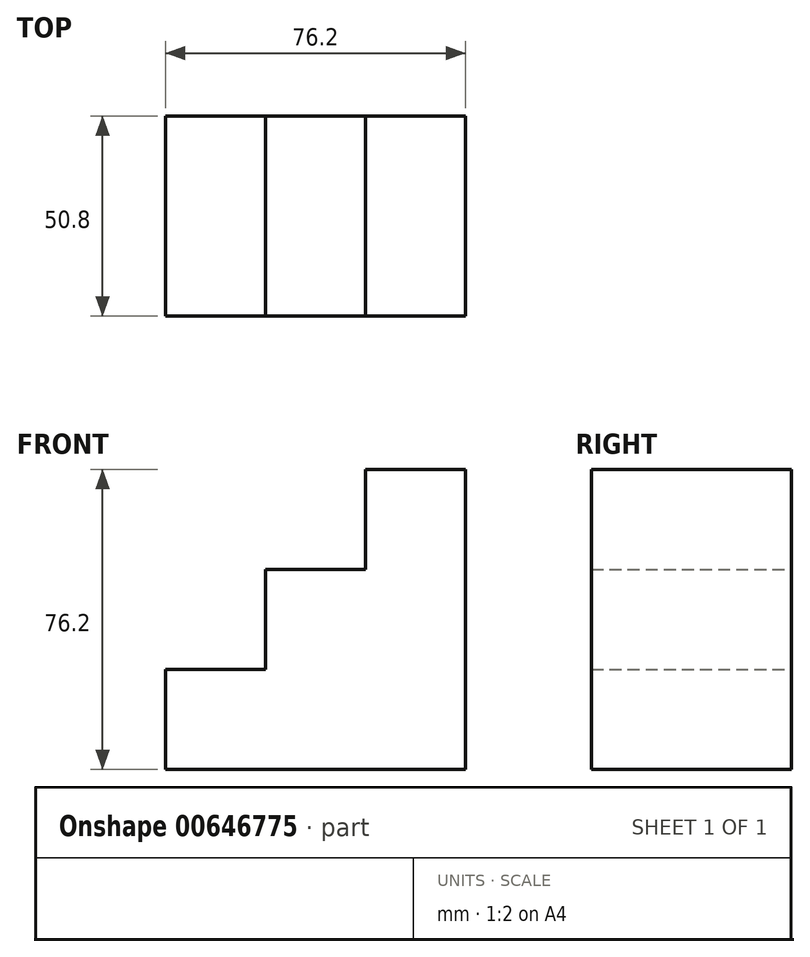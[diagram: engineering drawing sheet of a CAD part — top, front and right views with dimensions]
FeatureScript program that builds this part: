
annotation { "Feature Type Name" : "Feature", "Feature Type Description" : "" }
export const myFeature = defineFeature(function(context is Context, id is Id, definition is map)
    precondition{}
    {
        {
            var Q0;
            Q0=qCreatedBy(makeId("Front.planeOp"),FACE);
            var sketch = newSketch(context, id + "F0", { "sketchPlane" : qUnion([Q0])});
            skLineSegment(sketch, "E0", {"start": v(48.03, 47.46) * mm, "end": v(48.03, -28.74) * mm});
            skLineSegment(sketch, "E1", {"start": v(48.03, -28.74) * mm, "end": v(-28.17, -28.74) * mm});
            skLineSegment(sketch, "E2", {"start": v(-28.17, -28.74) * mm, "end": v(-28.17, -3.34) * mm});
            skLineSegment(sketch, "E3", {"start": v(-28.17, -3.34) * mm, "end": v(-2.77, -3.34) * mm});
            skLineSegment(sketch, "E4", {"start": v(-2.77, -3.34) * mm, "end": v(-2.77, 22.06) * mm});
            skLineSegment(sketch, "E5", {"start": v(-2.77, 22.06) * mm, "end": v(22.63, 22.06) * mm});
            skLineSegment(sketch, "E6", {"start": v(22.63, 22.06) * mm, "end": v(22.63, 47.46) * mm});
            skLineSegment(sketch, "E7", {"start": v(22.63, 47.46) * mm, "end": v(48.03, 47.46) * mm});
            skSolve(sketch);
        }
        {
            var Q0;
            Q0=makeQuery(id+"F0.imprint","IMPRINT",FACE,{"disambiguationData":[TD([[makeQuery(id+"F0.imprint","IMPRINT",EDGE,{"derivedFrom":sQuery(id+"F0.wireOp",EDGE,"E0")}),-1.0]])]});
            extrude(context, id + "F1", {"entities" : qUnion([Q0]), "depth" : 50.8 * mm, "offsetDistance" : 25.4 * mm});
        }
    });
